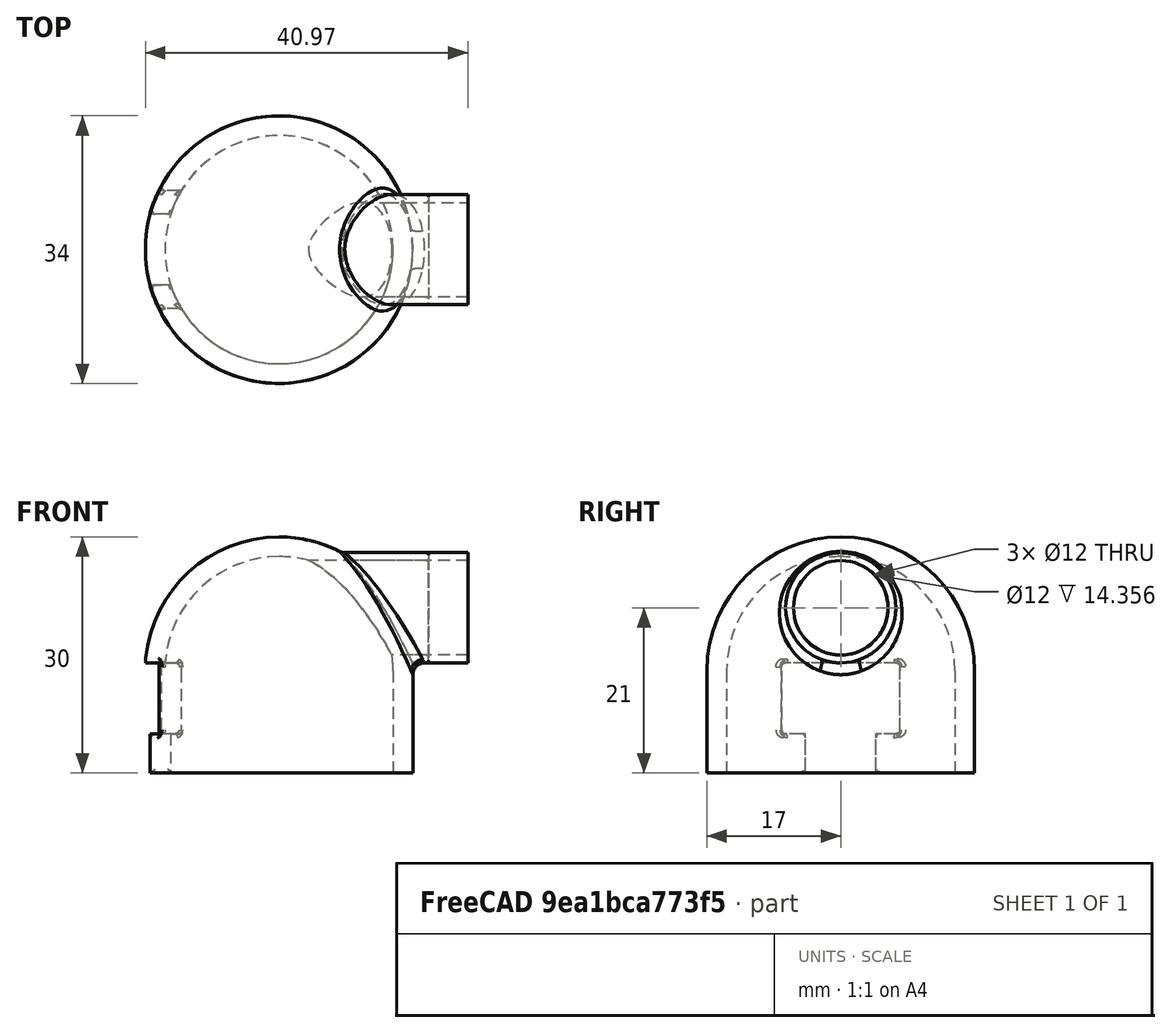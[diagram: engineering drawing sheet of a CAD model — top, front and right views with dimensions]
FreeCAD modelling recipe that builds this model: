
FCSTD DOCUMENT  (FreeCAD 0.16R)
Label: InstantPotDiverter4
License: All rights reserved
LicenseURL: http://en.wikipedia.org/wiki/All_rights_reserved
objects: Sketcher::SketchObject×4, PartDesign::Fillet×4, PartDesign::Pad×2, PartDesign::Revolution×1, Part::Cut×1, Part::FeaturePython×1, PartDesign::Pocket×1, Mesh::Feature×1
note: 18 computed .brp shape members not serialized (recipe doc carries the construction recipe); baked Part::Feature solids carry a one-line shape summary decoded from their .brp

FEATURE [Sketcher::SketchObject] Sketch
  Placement = pos=(0,0,0) rot=(1,0,0;1.5708rad)
  sketch-geometry (6):
    g0: LineSegment StartX=14.5 StartY=13 StartZ=0 EndX=14.5 EndY=0 EndZ=0
    g1: LineSegment StartX=14.5 StartY=0 StartZ=0 EndX=17 EndY=0 EndZ=0
    g2: LineSegment StartX=17 StartY=0 StartZ=0 EndX=17 EndY=13 EndZ=0
    g3: ArcOfCircle CenterX=0 CenterY=13 CenterZ=0 NormalX=0 NormalY=0 NormalZ=1 Radius=14.5 StartAngle=2.009e-09 EndAngle=1.5708
    g4: ArcOfCircle CenterX=0 CenterY=13 CenterZ=0 NormalX=0 NormalY=0 NormalZ=1 Radius=17 StartAngle=6.28319 EndAngle=7.85398
    g5: LineSegment StartX=0 StartY=30 StartZ=0 EndX=0 EndY=27.5 EndZ=0
  constraints (20):
    c: Vertical(g0)
    c: Coincident(g0,g1)
    c: Horizontal(g1)
    c: Coincident(g1,g2)
    c: Vertical(g2)
    c: Coincident(g3,g0)
    c: PointOnObject(g3,g-2)
    c: Coincident(g4,g3)
    c: Coincident(g4,g2)
    c: DistanceX(g1,g1) = 2.5
    c: PointOnObject(g4,g-2)
    c: PointOnObject(g1,g-1)
    c: Vertical(g5)
    c: Coincident(g5,g4)
    c: Coincident(g5,g3)
    c: Tangent(g0,g3)
    c: Tangent(g2,g4)
    c: DistanceX(g0) = 14.5
    c: DistanceY(g2) = 13
    c: Perpendicular(g4,g-2)
FEATURE [PartDesign::Revolution] Revolution  label="Body"
  Angle = 360
  Axis = (0,0,1)
  Base = (0,0,0)
  Placement = pos=(0,0,0) rot=(1,0,0;1.5708rad)
  ReferenceAxis = -> Sketch [V_Axis]
  Reversed = true
  Sketch = -> Sketch
FEATURE [Sketcher::SketchObject] Sketch001
  Placement = pos=(0,0,0) rot=(0.57735,0.57735,0.57735;2.0944rad)
  sketch-geometry (2):
    g0: Circle CenterX=0 CenterY=21 CenterZ=0 NormalX=0 NormalY=0 NormalZ=1 Radius=7
    g1: Circle CenterX=0 CenterY=21 CenterZ=0 NormalX=0 NormalY=0 NormalZ=1 Radius=6
  constraints (5):
    c: Radius(g0) = 7
    c: DistanceY(g-1,g0) = 21
    c: Coincident(g1,g0)
    c: PointOnObject(g0,g-2)
    c: Radius(g1) = 6
FEATURE [PartDesign::Pad] Pad  label="Spout"
  Length = 24
  Length2 = 1
  Placement = pos=(0,0,0) rot=(0.57735,0.57735,0.57735;2.0944rad)
  Sketch = -> Sketch001
  Type = 0
FEATURE [Sketcher::SketchObject] Sketch002
  Placement = pos=(0,0,0) rot=(0.57735,0.57735,0.57735;2.0944rad)
  sketch-geometry (8):
    g0: LineSegment StartX=-7.5 StartY=14 StartZ=0 EndX=7.5 EndY=14 EndZ=0
    g1: LineSegment StartX=7.5 StartY=14 StartZ=0 EndX=7.5 EndY=5 EndZ=0
    g2: LineSegment StartX=-7.5 StartY=5 StartZ=0 EndX=-7.5 EndY=14 EndZ=0
    g3: LineSegment StartX=-7.5 StartY=5 StartZ=0 EndX=-4.5 EndY=5 EndZ=0
    g4: LineSegment StartX=-4.5 StartY=5 StartZ=0 EndX=-4.5 EndY=-5 EndZ=0
    g5: LineSegment StartX=-4.5 StartY=-5 StartZ=0 EndX=4.5 EndY=-5 EndZ=0
    g6: LineSegment StartX=4.5 StartY=-5 StartZ=0 EndX=4.5 EndY=5 EndZ=0
    g7: LineSegment StartX=4.5 StartY=5 StartZ=0 EndX=7.5 EndY=5 EndZ=0
  constraints (23):
    c: Coincident(g0,g1)
    c: Coincident(g2,g0)
    c: Horizontal(g0)
    c: Vertical(g1)
    c: Vertical(g2)
    c: DistanceX(g0,g0) = 15
    c: DistanceY(g0) = 14
    c: Symmetric(g1,g2,g-2)
    c: Coincident(g2,g3)
    c: Horizontal(g3)
    c: Coincident(g3,g4)
    c: Vertical(g4)
    c: Coincident(g4,g5)
    c: Coincident(g5,g6)
    c: Coincident(g6,g7)
    c: Coincident(g7,g1)
    c: Distance(g3) = 3
    c: Distance(g7) = 3
    c: Vertical(g6)
    c: Horizontal(g5)
    c: DistanceY(g4) = -5
    c: DistanceY(g3) = 5
    c: Horizontal(g7)
FEATURE [PartDesign::Pad] Pad001  label="Slot"
  Length = 20
  Length2 = 100
  Placement = pos=(0,0,0) rot=(0.57735,0.57735,0.57735;2.0944rad)
  Reversed = true
  Sketch = -> Sketch002
  Type = 0
FEATURE [Part::Cut] Cut
  Base = -> Revolution
  Tool = -> Pad001
FEATURE [Part::FeaturePython] Connect  # WARN: FeaturePython — macro-defined, semantics opaque (R4)
  Base = -> Pad
  Mode = 1
  Tool = -> Cut
FEATURE [Sketcher::SketchObject] Sketch003
  ExternalGeometry = -> [Connect]
  Placement = pos=(24,0,0) rot=(0.57735,0.57735,0.57735;2.0944rad)
  Support = -> Connect [Face1]
  sketch-geometry (1):
    g0: Circle CenterX=0 CenterY=21 CenterZ=0 NormalX=0 NormalY=0 NormalZ=1 Radius=8
  constraints (2):
    c: Coincident(g-3,g0)
    c: Radius(g0) = 8
FEATURE [PartDesign::Pocket] Pocket
  Length = 5
  Sketch = -> Sketch003
  Type = 0
FEATURE [PartDesign::Fillet] Fillet
  Base = -> Pocket [Edge5,Edge14]
  Radius = 0.29
FEATURE [PartDesign::Fillet] Fillet001
  Base = -> Fillet [Edge17,Edge18,Edge19,Edge20,Edge8,Edge21,Edge46,Edge34,Edge50,Edge33,Edge56,Edge47,Edge53,Edge54,Edge29,Edge27,Edge52,Edge55,Edge30,Edge24,Edge25,Edge23,Edge10,Edge26,Edge22,Edge9]
  Radius = 0.5
FEATURE [PartDesign::Fillet] Fillet002
  Base = -> Fillet001 [Edge42,Edge44,Edge45,Edge33,Edge47,Edge17]
  Radius = 0.2
FEATURE [PartDesign::Fillet] Fillet003
  Base = -> Fillet002 [Edge20]
  Radius = 1.5
FEATURE [Mesh::Feature] Mesh  label="Fillet003 (Meshed)"
